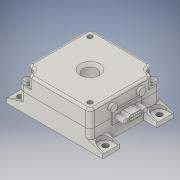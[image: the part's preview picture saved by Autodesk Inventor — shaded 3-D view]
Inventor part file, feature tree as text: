
AUTODESK INVENTOR PART (.ipt)
format: ipt  version: 2018 (Build 220112000, 112)  size: 405,504 bytes
history: native  units: in
note: dims shown in document units (in); Inventor stores cm internally (conversion verified against a paired STEP export)
features: extrude x11, sketch x11, chamfer x5, thread x4, fillet x3, plane x2, split x1
ambient origin geometry x8: Origin, YZ Plane, XZ Plane, XY Plane, X Axis, Y Axis, Z Axis, Center Point
bodies: Solid1 (feature_tree)
feature tree (37):
  extrude  "Extrusion1"  Depth=1.9685in
  sketch  "Sketch2"  dims[d2=0.9843in d3=0.0in d4=0.4724in]
  extrude  "Extrusion2"  Depth=0.4724in
  chamfer  "Chamfer1"  Distance=0.1181in Angle=45.0deg
  chamfer  "Chamfer2"  Distance=0.1181in Angle=45.0deg
  chamfer  "Chamfer3"  Distance=0.1181in Angle=45.0deg
  chamfer  "Chamfer4"  Distance=0.1181in Angle=45.0deg
  plane  "Work Plane1"
  extrude  "Extrusion3"  Depth=0.1575in
  extrude  "Extrusion4"  Depth=0.2362in
  extrude  "Extrusion5"  Depth=0.1575in
  chamfer  "Chamfer5"  Distance=0.1575in
  extrude  "Extrusion6"  Depth=0.1575in
  extrude  "Extrusion7"  Depth=0.2362in
  fillet  "Fillet1"  Radius=0.1575in
  fillet  "Fillet2"  Radius=0.3543in
  extrude  "Extrusion8"  Depth=0.1181in TaperAngle=0.0deg
  extrude  "Extrusion9"  Depth=0.9843in
  extrude  "Extrusion10"  Depth=0.9843in
  extrude  "Extrusion11"  Depth=0.3937in
  fillet  "Fillet3"  Radius=0.3937in
  plane  "Work Plane2"
  split  "Split1"
  thread  "Thread1"  [1 undecoded]
  thread  "Thread2"  [1 undecoded]
  thread  "Thread3"  [1 undecoded]
  thread  "Thread4"  [1 undecoded]
  sketch  "Sketch1"  dims[d0=1.9685in d1=1.9685in]
  sketch  "Sketch3"  dims[d5=0.2362in]
  sketch  "Sketch4"  dims[d6=0.4724in]
  sketch  "Sketch5"  dims[d7=0.2362in]
  sketch  "Sketch7"  dims[d8=0.3543in d9=2.3228in d10=0.0in d11=0.0in d12=0.1181in d13=0.3543in d14=45.0deg d15=0.1181in d16=0.3543in d17=45.0deg d18=0.1181in d19=0.3543in d20=45.0deg d21=0.1181in d22=0.3543in d23=45.0deg]
  sketch  "Sketch8"  dims[d24=-0.2362in d25=0.1575in]
  sketch  "Sketch9"  dims[d26=0.1575in d27=0.2362in]
  sketch  "Sketch10"  dims[d28=0.1575in d29=0.1575in]
  sketch  "Sketch11"  dims[d30=0.1575in]
  sketch  "Sketch12"  dims[d31=0.2362in d32=0.1575in d34=0.1575in d35=0.2362in d36=0.1575in d37=0.3543in d38=0.0in d40=0.1181in d41=0.0in d42=0.9843in d43=0.9843in d44=0.3937in d45=0.3937in d46=0.0in d48=0.0787in d49=0.0787in d50=45.0deg d51=0.2362in d52=0.2362in d53=0.2362in d54=0.2362in d55=0.315in d56=0.0in d57=0.1969in d58=0.1181in d59=0.1181in d60=0.1969in d61=0.1181in d62=0.1181in d63=0.0787in d64=0.0in d65=0.1181in d66=0.0591in d67=0.5906in d68=0.7874in d69=0.315in d70=0.3504in d71=0.0394in d72=0.0in d73=0.1181in d74=0.1181in d76=0.1181in d77=0.1181in d78=0.1181in d79=0.2362in d81=0.1575in d82=0.1575in d83=0.1575in d84=0.1575in d85=0.0394in d86=0.0394in d87=0.0394in d88=0.0394in d89=0.0394in d90=0.0197in d91=0.2362in d92=0.0in d93=0.1969in d94=0.1969in d95=0.1181in d96=0.1181in d97=0.0in d98=0.0in d99=0.0787in d100=0.0in d101=0.1181in d102=0.1181in d103=0.3937in d104=0.3937in d105=0.1969in d106=0.1969in d107=0.1969in d108=0.0in d109=0.0098in d112=-0.5118in d113=0.3937in d114=0.0in d115=0.3937in d116=0.0in d117=0.3937in d118=0.0in d119=0.3937in d120=0.0in d121=0.2362in]
note: 4 required parameter values undecoded (feature->parameter linkage not recoverable at this tier; creation-order binding heuristic only, values carry confidence <= 0.55)
